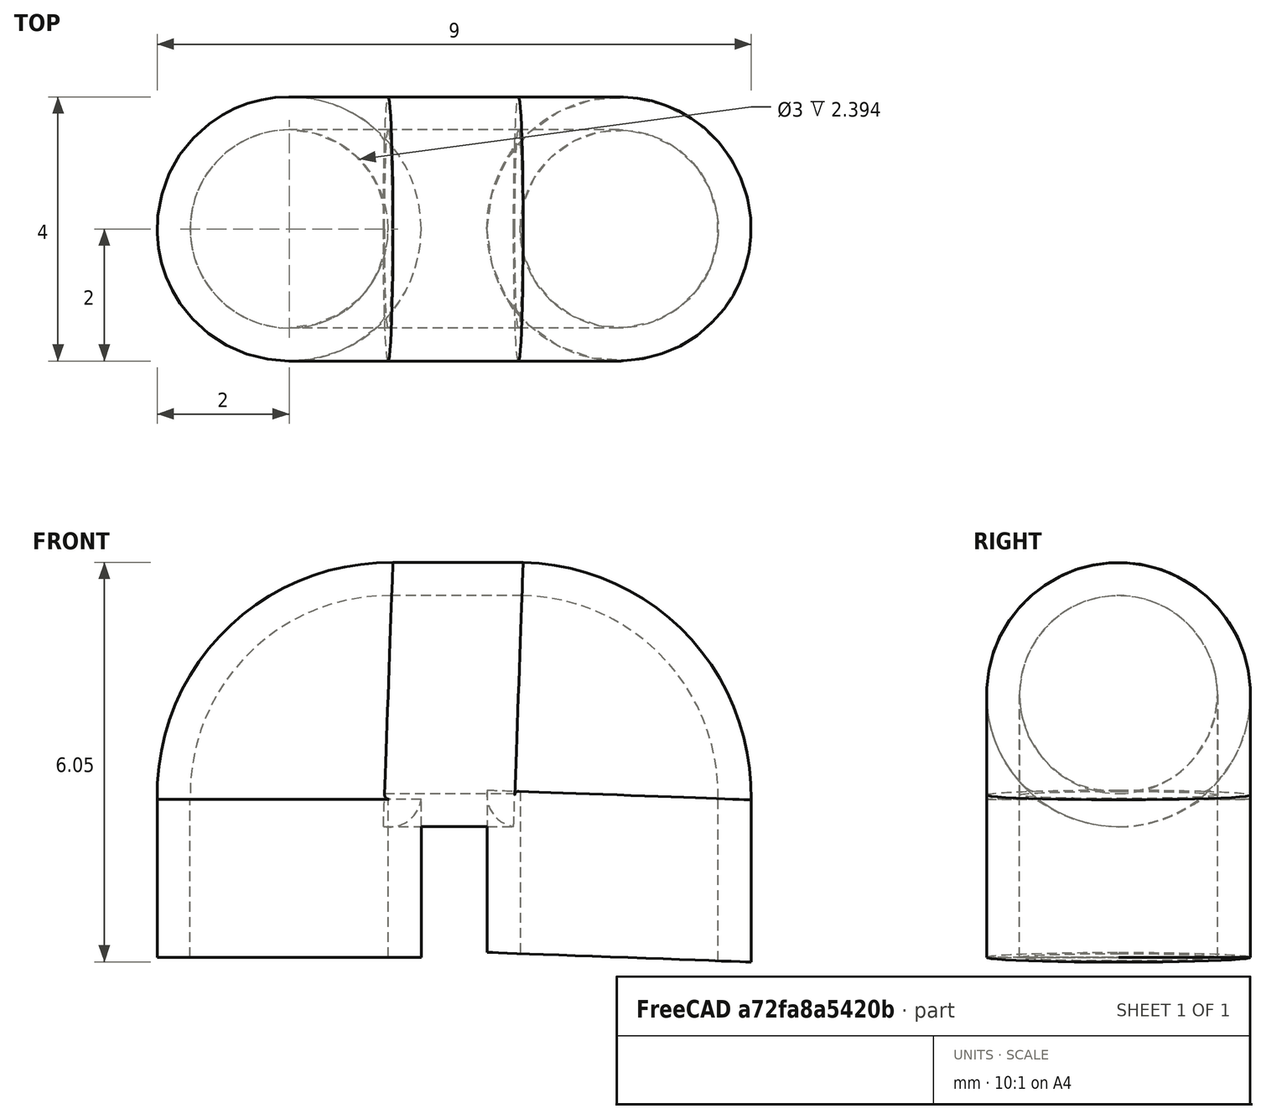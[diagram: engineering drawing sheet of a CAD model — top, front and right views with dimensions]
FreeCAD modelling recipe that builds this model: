
FCSTD DOCUMENT  (FreeCAD 0.19R24291 (Git))
Label: bush_simply02
License: All rights reserved
LicenseURL: http://en.wikipedia.org/wiki/All_rights_reserved
objects: Sketcher::SketchObject×2, PartDesign::AdditivePipe×1, PartDesign::Body×1
note: 5 computed .brp shape members not serialized (recipe doc carries the construction recipe); baked Part::Feature solids carry a one-line shape summary decoded from their .brp

FEATURE [Sketcher::SketchObject] Sketch
  FullyConstrained = true
  MapMode = 5
  Support = -> [XY_Plane]
  sketch-geometry (2):
    g0: Circle CenterX=0 CenterY=0 CenterZ=0 NormalX=0 NormalY=0 NormalZ=1 AngleXU=0 Radius=2
    g1: Circle CenterX=0 CenterY=0 CenterZ=0 NormalX=0 NormalY=0 NormalZ=1 AngleXU=0 Radius=1.5
  constraints (4):
    c: Coincident(g0,g-1)
    c: Coincident(g1,g0)
    c: Radius(g0) = 2
    c: Radius(g1) = 1.5
FEATURE [Sketcher::SketchObject] Sketch001
  FullyConstrained = false
  MapMode = 5
  Placement = pos=(0,0,0) rot=(1,0,0;1.5708rad)
  Support = -> [XZ_Plane]
  sketch-geometry (5):
    g0: LineSegment StartX=0 StartY=0 StartZ=0 EndX=0 EndY=2.3937 EndZ=0
    g1: LineSegment StartX=1.50005 StartY=3.97795 StartZ=0 EndX=3.47386 EndY=3.97795 EndZ=0
    g2: LineSegment StartX=5 StartY=2.45766 StartZ=0 EndX=5 EndY=0 EndZ=0
    g3: ArcOfCircle CenterX=1.51411 CenterY=2.46235 CenterZ=0 NormalX=0 NormalY=0 NormalZ=1 AngleXU=0 Radius=1.51567 StartAngle=1.58007 EndAngle=3.1869
    g4: ArcOfCircle CenterX=3.47743 CenterY=2.45538 CenterZ=0 NormalX=0 NormalY=0 NormalZ=1 AngleXU=0 Radius=1.52258 StartAngle=0.0014924 EndAngle=1.57314
  constraints (10):
    c: Coincident(g0,g-1)
    c: Horizontal(g1)
    c: PointOnObject(g2,g-1)
    c: Vertical(g2)
    c: Parallel(g2,g0)
    c: Distance(g0,g2) = 5
    c: Coincident(g3,g0)
    c: Coincident(g3,g1)
    c: Coincident(g4,g1)
    c: Coincident(g4,g2)
FEATURE [PartDesign::AdditivePipe] AdditivePipe
  AuxilleryCurvelinear = true
  AuxillerySpineTangent = false
  Binormal = (0,0,0)
  Mode = 0
  Profile = -> Sketch
  Spine = -> Sketch001 [Edge1,Edge2,Edge3,Edge4,Edge5]
  SpineTangent = false
  Transformation = 0
  Transition = 0
FEATURE [PartDesign::Body] Body
  Group = -> [Sketch,Sketch001,AdditivePipe]
  Origin = -> Origin
  Tip = -> AdditivePipe
